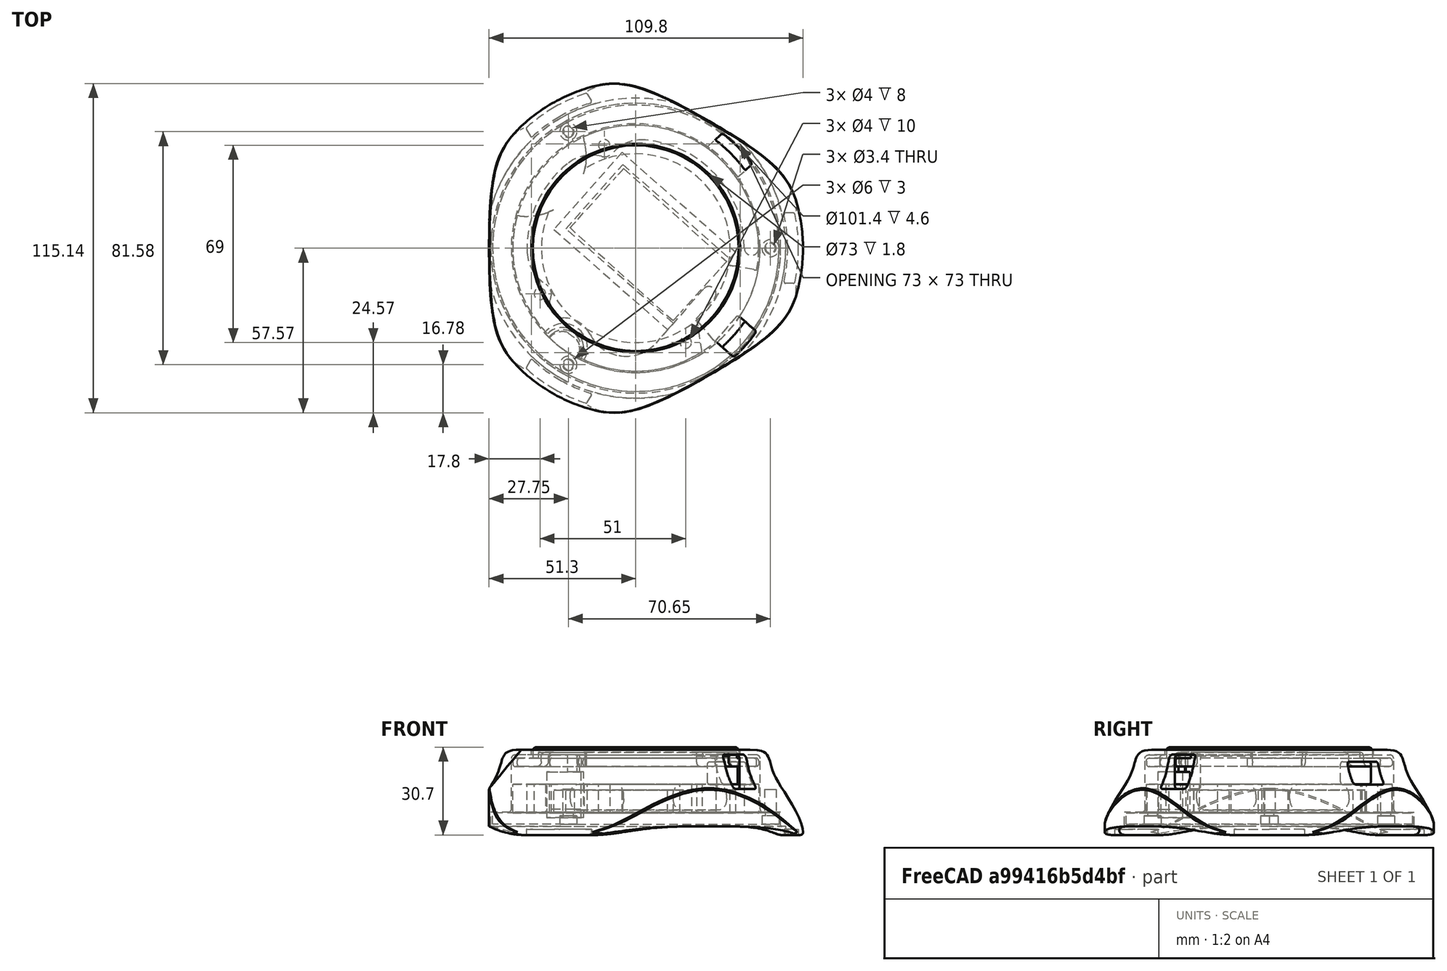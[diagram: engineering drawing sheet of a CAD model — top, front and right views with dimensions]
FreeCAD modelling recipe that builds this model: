
FCSTD DOCUMENT  (FreeCAD 1.0R39109 (Git))
Label: slimCasing
License: All rights reserved
LicenseURL: https://en.wikipedia.org/wiki/All_rights_reserved
objects: Sketcher::SketchObject×15, PartDesign::Pocket×9, PartDesign::Pad×6, PartDesign::SubShapeBinder×5, PartDesign::Body×4, PartDesign::Plane×4, Mesh::Feature×1, PartDesign::Revolution×1, PartDesign::Fillet×1, PartDesign::AdditivePipe×1, PartDesign::Mirrored×1, PartDesign::PolarPattern×1
note: 101 computed .brp shape members not serialized (recipe doc carries the construction recipe); baked Part::Feature solids carry a one-line shape summary decoded from their .brp

FEATURE [Sketcher::SketchObject] Sketch
  ArcFitTolerance = 1e-06
  AttachmentSupport = -> [XZ_Plane]
  FullyConstrained = true
  MakeInternals = false
  MapMode = 5
  Placement = pos=(0,0,0) rot=(1,0,0;1.5708rad)
  sketch-geometry (17):
    g0: LineSegment StartX=-36 StartY=12 StartZ=0 EndX=-36 EndY=9.5 EndZ=0
    g1: LineSegment StartX=-36 StartY=9.5 StartZ=0 EndX=-42 EndY=9.5 EndZ=0
    g2: LineSegment StartX=-43 StartY=8.5 StartZ=0 EndX=-43 EndY=7.5 EndZ=0
    g3: LineSegment StartX=-42 StartY=6.5 StartZ=0 EndX=-34.8 EndY=6.5 EndZ=0
    g4: LineSegment StartX=-33 StartY=8.3 StartZ=0 EndX=-33 EndY=10.2 EndZ=0
    g5: LineSegment StartX=-31.7 StartY=11.5 StartZ=0 EndX=0 EndY=11.5 EndZ=0
    g6: LineSegment StartX=0 StartY=11.5 StartZ=0 EndX=0 EndY=13.3 EndZ=0
    g7: ArcOfCircle CenterX=-34.7 CenterY=12 CenterZ=0 NormalX=0 NormalY=0 NormalZ=1 AngleXU=0 Radius=1.3 StartAngle=1.5708 EndAngle=3.14159
    g8: ArcOfCircle CenterX=-31.7 CenterY=10.2 CenterZ=0 NormalX=0 NormalY=0 NormalZ=1 AngleXU=0 Radius=1.3 StartAngle=1.5708 EndAngle=3.14159
    g9: GeomPoint [constr] X=-33 Y=11.5 Z=0
    g10: GeomPoint [constr] X=-36 Y=9.5 Z=0
    g11: ArcOfCircle CenterX=-34.8 CenterY=8.3 CenterZ=0 NormalX=0 NormalY=0 NormalZ=1 AngleXU=0 Radius=1.8 StartAngle=4.71239 EndAngle=6.28319
    g12: GeomPoint [constr] X=-33 Y=6.5 Z=0
    g13: ArcOfCircle CenterX=-42 CenterY=8.5 CenterZ=0 NormalX=0 NormalY=0 NormalZ=1 AngleXU=0 Radius=1 StartAngle=1.5708 EndAngle=3.14159
    g14: GeomPoint [constr] X=-43 Y=9.5 Z=0
    g15: ArcOfCircle CenterX=-42 CenterY=7.5 CenterZ=0 NormalX=0 NormalY=0 NormalZ=1 AngleXU=0 Radius=1 StartAngle=3.14159 EndAngle=4.71239
    g16: LineSegment StartX=-34.7 StartY=13.3 StartZ=0 EndX=0 EndY=13.3 EndZ=0
  constraints (41):
    c: Vertical(g0)
    c: Horizontal(g1)
    c: Vertical(g2)
    c: Horizontal(g3)
    c: Vertical(g4)
    c: Horizontal(g5)
    c: Coincident(g5,g6)
    c: Vertical(g6)
    c: DistanceY(g10,g9) = 2
    c: Distance(g10,g14) = 7
    c: DistanceX(g10,g9) = 3
    c: DistanceX(g9,g5) = 33
    c: DistanceY(g-1,g5) = 11.5
    c: Tangent(g0,g7) = -1.5708
    c: PointOnObject(g9,g4)
    c: PointOnObject(g9,g5)
    c: Tangent(g4,g8) = 1.5708
    c: Tangent(g5,g8) = 1.5708
    c: PointOnObject(g12,g3)
    c: PointOnObject(g12,g4)
    c: Tangent(g3,g11) = -1.5708
    c: Tangent(g4,g11) = -1.5708
    c: PointOnObject(g14,g2)
    c: PointOnObject(g14,g1)
    c: Tangent(g2,g13) = -1.5708
    c: Tangent(g1,g13) = -1.5708
    c: Tangent(g2,g15) = -1.5708
    c: Tangent(g3,g15) = -1.5708
    c: Equal(g7,g8)
    c: Coincident(g1,g10)
    c: Coincident(g0,g1)
    c: DistanceY(g0,g0) = 2.5
    c: Radius(g11) = 1.8
    c: Equal(g13,g15)
    c: Radius(g13) = 1
    c: PointOnObject(g5,g-2)
    c: DistanceY(g3,g1) = 3
    c: DistanceY(g7,g7) = 1.3
    c: Horizontal(g16)
    c: Coincident(g6,g16)
    c: Tangent(g7,g16) = 1.5708
FEATURE [Mesh::Feature] PCB_Board  label="PCB Board"
  Placement = pos=(-64.6,63.9,0) rot=(0,0,1;0rad)
FEATURE [PartDesign::Revolution] Revolution
  Angle = 360
  Angle2 = 60
  Axis = (0,2e-16,1)
  Base = (0,0,0)
  Placement = pos=(0,0,0) rot=(1,0,0;1.5708rad)
  Profile = -> Sketch
  ReferenceAxis = -> Sketch [V_Axis]
  Refine = true
  Suppressed = false
  Type = 0
FEATURE [Sketcher::SketchObject] Sketch001
  ArcFitTolerance = 1e-06
  AttachmentSupport = -> [Revolution]
  FullyConstrained = false
  MakeInternals = false
  MapMode = 5
  Placement = pos=(0,1.4e-15,6.5) rot=(1,0,0;3.14159rad)
  sketch-geometry (12):
    g0: ArcOfCircle CenterX=25.2748 CenterY=34.7877 CenterZ=0 NormalX=0 NormalY=0 NormalZ=1 AngleXU=0 Radius=6.2 StartAngle=2.58543 EndAngle=5.58271
    g1: ArcOfCircle CenterX=0 CenterY=0 CenterZ=0 NormalX=0 NormalY=0 NormalZ=1 AngleXU=0 Radius=43 StartAngle=0.798167 EndAngle=1.08679
    g2: LineSegment [constr] StartX=25.2748 StartY=34.7877 StartZ=0 EndX=0 EndY=0 EndZ=0
    g3: ArcOfCircle CenterX=-42.4024 CenterY=26.496 CenterZ=0 NormalX=0 NormalY=0 NormalZ=1 AngleXU=0 Radius=21 StartAngle=4.70073 EndAngle=6.74863
    g4: ArcOfCircle CenterX=0 CenterY=0 CenterZ=0 NormalX=0 NormalY=0 NormalZ=1 AngleXU=0 Radius=43 StartAngle=2.15278 EndAngle=3.0134
    g5: LineSegment [constr] StartX=0 StartY=0 StartZ=0 EndX=-42.4024 EndY=26.496 EndZ=0
    g6: LineSegment [constr] StartX=0 StartY=0 StartZ=0 EndX=31.9552 EndY=-28.7726 EndZ=0
    g7: LineSegment StartX=39.7845 StartY=-16.3155 StartZ=0 EndX=30.5323 EndY=-12.5212 EndZ=0
    g8: LineSegment StartX=20.3847 StartY=-37.8611 StartZ=0 EndX=15.6441 EndY=-29.0562 EndZ=0
    g9: ArcOfCircle CenterX=0 CenterY=0 CenterZ=0 NormalX=0 NormalY=0 NormalZ=1 AngleXU=0 Radius=33 StartAngle=5.20629 EndAngle=5.894
    g10: ArcOfCircle CenterX=0 CenterY=0 CenterZ=0 NormalX=0 NormalY=0 NormalZ=1 AngleXU=0 Radius=43 StartAngle=5.20629 EndAngle=5.894
    g11: LineSegment [constr] StartX=15.6441 StartY=-29.0562 StartZ=0 EndX=30.5323 EndY=-12.5212 EndZ=0
  constraints (20):
    c: Coincident(g1,g0)
    c: Coincident(g1,g0)
    c: Coincident(g2,g0)
    c: Angle(g-1,g2) = 0.942478
    c: Coincident(g4,g3)
    c: Coincident(g4,g3)
    c: Radius(g3) = 21
    c: Coincident(g5,g3)
    c: Distance(g5,g5) = 50
    c: Angle(g5,g-1) = 0.558505
    c: Coincident(g9,g7)
    c: Coincident(g9,g8)
    c: Distance(g7,g7) = 10
    c: Angle(g6,g-1) = 0.733038
    c: Coincident(g10,g7)
    c: Coincident(g10,g8)
    c: Coincident(g11,g8)
    c: Coincident(g11,g7)
    c: Perpendicular(g6,g11)
    c: Distance(g11,g11) = 22.25
FEATURE [Sketcher::SketchObject] Sketch027
  ArcFitTolerance = 0
  FullyConstrained = true
  MakeInternals = false
  MapMode = 5
  sketch-geometry (4):
    g0: LineSegment StartX=-24.25 StartY=14 StartZ=0 EndX=24.25 EndY=14 EndZ=0
    g1: LineSegment StartX=24.25 StartY=14 StartZ=0 EndX=24.25 EndY=-14 EndZ=0
    g2: LineSegment StartX=24.25 StartY=-14 StartZ=0 EndX=-24.25 EndY=-14 EndZ=0
    g3: LineSegment StartX=-24.25 StartY=-14 StartZ=0 EndX=-24.25 EndY=14 EndZ=0
  constraints (11):
    c: Coincident(g0,g1)
    c: Coincident(g1,g2)
    c: Coincident(g2,g3)
    c: Coincident(g3,g0)
    c: Horizontal(g0)
    c: Horizontal(g2)
    c: Vertical(g1)
    c: Vertical(g3)
    c: Symmetric(g0,g1,g-1)
    c: DistanceX(g0,g0) = 48.5
    c: DistanceY(g1,g1) = 28
FEATURE [PartDesign::Pad] Pad004
  Direction = (0,0,1)
  Length = 9
  Length2 = 10
  Profile = -> Sketch027
  ReferenceAxis = -> Sketch027 [N_Axis]
  Suppressed = false
  Type = 0
FEATURE [PartDesign::Fillet] Fillet002
  Base = -> Pad004 [Edge4,Edge3,Edge10,Edge9]
  BaseFeature = -> Pad004
  Radius = 4
  SupportTransform = false
  Suppressed = false
  UseAllEdges = false
FEATURE [PartDesign::Body] Body005  label="Batterie"
  AllowCompound = false
  Group = -> [Sketch027,Pad004,Fillet002]
  Placement = pos=(4.42123,1.23614,-9.3) rot=(0,0,1;5.5484rad)
  Tip = -> Fillet002
FEATURE [Sketcher::SketchObject] Sketch032
  ArcFitTolerance = 1e-06
  FullyConstrained = false
  MakeInternals = false
  MapMode = 5
  sketch-geometry (34):
    g0: Circle CenterX=17.5 CenterY=-33 CenterZ=0 NormalX=0 NormalY=0 NormalZ=1 AngleXU=0 Radius=2
    g1: Circle CenterX=-33.5 CenterY=-16 CenterZ=0 NormalX=0 NormalY=0 NormalZ=1 AngleXU=0 Radius=2
    g2: Circle CenterX=-11 CenterY=36 CenterZ=0 NormalX=0 NormalY=0 NormalZ=1 AngleXU=0 Radius=2
    g3: Circle [constr] CenterX=0 CenterY=0 CenterZ=0 NormalX=0 NormalY=0 NormalZ=1 AngleXU=0 Radius=32.5
    g4: Circle [constr] CenterX=0 CenterY=0 CenterZ=0 NormalX=0 NormalY=0 NormalZ=1 AngleXU=0 Radius=43
    g5: GeomPoint [constr] X=-11 Y=36 Z=0
    g6: LineSegment [constr] StartX=-12.5654 StartY=41.1231 StartZ=0 EndX=0 EndY=0 EndZ=0
    g7: LineSegment [constr] StartX=0 StartY=0 StartZ=0 EndX=-38.8021 EndY=-18.5309 EndZ=0
    g8: GeomPoint [constr] X=-33.5 Y=-16 Z=0
    g9: GeomPoint [constr] X=17.5 Y=-33 Z=0
    g10: LineSegment [constr] StartX=20.1456 StartY=-37.9889 StartZ=0 EndX=0 EndY=0 EndZ=0
    g11: ArcOfCircle CenterX=0 CenterY=0 CenterZ=0 NormalX=0 NormalY=0 NormalZ=1 AngleXU=0 Radius=43 StartAngle=4.27973 EndAngle=5.28201
    g12: ArcOfCircle CenterX=-25.2748 CenterY=-34.7877 CenterZ=0 NormalX=0 NormalY=0 NormalZ=1 AngleXU=0 Radius=8.4 StartAngle=5.7527 EndAngle=8.69863
    g13: ArcOfCircle CenterX=-25.2748 CenterY=-34.7877 CenterZ=0 NormalX=0 NormalY=0 NormalZ=1 AngleXU=0 Radius=10.4 StartAngle=0.461307 EndAngle=1.57014
    g14: ArcOfCircle CenterX=0 CenterY=0 CenterZ=0 NormalX=0 NormalY=0 NormalZ=1 AngleXU=0 Radius=43 StartAngle=1e-16 EndAngle=3.88841
    g15: LineSegment [constr] StartX=0 StartY=0 StartZ=0 EndX=-25.2748 EndY=-34.7877 EndZ=0
    g16: ArcOfCircle [constr] CenterX=0 CenterY=0 CenterZ=0 NormalX=0 NormalY=0 NormalZ=1 AngleXU=0 Radius=38 StartAngle=1.48247 EndAngle=5.30728
    g17: ArcOfCircle CenterX=-11 CenterY=36 CenterZ=0 NormalX=0 NormalY=0 NormalZ=1 AngleXU=0 Radius=4 StartAngle=4.4615 EndAngle=5.55637
    g18: ArcOfCircle CenterX=-15.3694 CenterY=18.951 CenterZ=0 NormalX=0 NormalY=0 NormalZ=1 AngleXU=0 Radius=13.6 StartAngle=1.31991 EndAngle=2.25221
    g19: ArcOfCircle CenterX=-33.5 CenterY=-16 CenterZ=0 NormalX=0 NormalY=0 NormalZ=1 AngleXU=0 Radius=4 StartAngle=5.8858 EndAngle=7.30937
    g20: ArcOfCircle CenterX=-24.3816 CenterY=-0.946243 CenterZ=0 NormalX=0 NormalY=0 NormalZ=1 AngleXU=0 Radius=13.6 StartAngle=3.18038 EndAngle=4.16777
    g21: ArcOfCircle CenterX=0 CenterY=0 CenterZ=0 NormalX=0 NormalY=0 NormalZ=1 AngleXU=0 Radius=38 StartAngle=2.25221 EndAngle=3.18038
    g22: ArcOfCircle CenterX=-25.2647 CenterY=-19.4565 CenterZ=0 NormalX=0 NormalY=0 NormalZ=1 AngleXU=0 Radius=4.93127 StartAngle=2.74421 EndAngle=4.71173
    g23: ArcOfCircle CenterX=-3.17343 CenterY=-24.1928 CenterZ=0 NormalX=0 NormalY=0 NormalZ=1 AngleXU=0 Radius=13.6 StartAngle=4.58196 EndAngle=5.56057
    g24: ArcOfCircle CenterX=-3.78345 CenterY=-24.1049 CenterZ=0 NormalX=0 NormalY=0 NormalZ=1 AngleXU=0 Radius=13.6 StartAngle=3.6029 EndAngle=4.5567
    g25: ArcOfCircle CenterX=0 CenterY=0 CenterZ=0 NormalX=0 NormalY=0 NormalZ=1 AngleXU=0 Radius=38 StartAngle=4.5567 EndAngle=4.58196
    g26: ArcOfCircle CenterX=0 CenterY=0 CenterZ=0 NormalX=0 NormalY=0 NormalZ=1 AngleXU=0 Radius=38 StartAngle=1e-16 EndAngle=1.48247
    g27: ArcOfCircle CenterX=40.5 CenterY=4.4e-15 CenterZ=0 NormalX=0 NormalY=0 NormalZ=1 AngleXU=0 Radius=2.5 StartAngle=3.14159 EndAngle=6.28319
    g28: ArcOfCircle CenterX=2.15235 CenterY=24.3049 CenterZ=0 NormalX=0 NormalY=0 NormalZ=1 AngleXU=0 Radius=13.6 StartAngle=1.48247 EndAngle=2.41477
    g29: LineSegment [constr] StartX=40.5 StartY=4.4e-15 StartZ=0 EndX=0 EndY=0 EndZ=0
    g30: LineSegment StartX=23.1906 StartY=-36.2104 StartZ=0 EndX=21.3491 EndY=-24.5044 EndZ=0
    g31: LineSegment StartX=21.3491 StartY=-24.5044 StartZ=0 EndX=27.4734 EndY=-17.5584 EndZ=0
    g32: ArcOfCircle CenterX=25.5982 CenterY=-15.905 CenterZ=0 NormalX=0 NormalY=0 NormalZ=1 AngleXU=0 Radius=2.5 StartAngle=5.56057 EndAngle=8.70217
    g33: LineSegment StartX=23.723 StartY=-14.2517 StartZ=0 EndX=7.02767 EndY=-33.1871 EndZ=0
  constraints (84):
    c: Equal(g0,g2)
    c: Equal(g2,g1)
    c: Diameter(g2) = 4
    c: DistanceX(g1,g-1) = 33.5
    c: DistanceY(g1,g-1) = 16
    c: DistanceX(g2) = -11
    c: DistanceY(g2) = 36
    c: DistanceX(g0) = 17.5
    c: DistanceY(g0) = -33
    c: Coincident(g3,g-1)
    c: Coincident(g4,g3)
    c: Diameter(g4) = 86
    c: Diameter(g3) = 65
    c: Coincident(g2,g5)
    c: PointOnObject(g6,g4)
    c: Coincident(g6,g3)
    c: PointOnObject(g2,g6)
    c: Coincident(g7,g3)
    c: PointOnObject(g7,g4)
    c: Coincident(g8,g1)
    c: Coincident(g9,g0)
    c: PointOnObject(g10,g4)
    c: Coincident(g10,g3)
    c: PointOnObject(g0,g10)
    c: PointOnObject(g11,g4)
    c: Distance(g23,g4) = 5
    c: Coincident(g11,g3)
    c: PointOnObject(g12,g4)
    c: Coincident(g12,g11)
    c: PointOnObject(g12,g4)
    c: Coincident(g13,g12)
    c: Coincident(g14,g3)
    c: Coincident(g14,g12)
    c: Distance(g12,g13) = 2
    c: Radius(g12) = 8.4
    c: Coincident(g15,g3)
    c: Coincident(g15,g12)
    c: Angle(g-1,g15) = 0.942478
    c: Coincident(g16,g3)
    c: Coincident(g17,g2)
    c: PointOnObject(g18,g16)
    c: PointOnObject(g23,g16)
    c: Tangent(g18,g17) = 1.5708
    c: Coincident(g19,g1)
    c: Distance(g19,g1) = 2
    c: Tangent(g20,g19) = 1.5708
    c: Coincident(g21,g3)
    c: Tangent(g21,g20) = -1.5708
    c: Tangent(g21,g18) = -1.5708
    c: Tangent(g22,g13) = 1.5708
    c: Tangent(g22,g19) = 1.5708
    c: Coincident(g25,g3)
    c: Tangent(g24,g13) = 1.5708
    c: Tangent(g25,g24) = -1.5708
    c: Equal(g23,g24)
    c: Equal(g24,g20)
    c: Equal(g20,g18)
    c: Radius(g18) = 13.6
    c: Tangent(g25,g23) = -1.5708
    c: Tangent(g22,g20)
    c: Coincident(g26,g3)
    c: Coincident(g26,g16)
    c: Tangent(g27,g26) = 1.5708
    c: Tangent(g27,g14) = -1.5708
    c: Coincident(g28,g16)
    c: Tangent(g26,g28)
    c: Equal(g28,g18)
    c: Coincident(g29,g27)
    c: Coincident(g29,g3)
    c: Angle(g29,g-2) = 1.5708
    c: Tangent(g28,g17) = 1.5708
    c: Distance(g17,g2) = 2
    c: Coincident(g31,g30)
    c: Tangent(g31,g32) = -1.5708
    c: PointOnObject(g30,g3)
    c: Tangent(g33,g23) = 1.5708
    c: Tangent(g33,g32) = -1.5708
    c: Coincident(g11,g30)
    c: Parallel(g31,g33)
    c: DistanceX(g32) = 25.5982
    c: DistanceY(g32) = -15.905
    c: Distance(g33,g31) = 5
    c: Angle(g-2,g30) = 0.156032
    c: Distance(g30,g30) = 11.85
FEATURE [PartDesign::Pad] Pad007
  Direction = (0,0,1)
  Length = 10
  Length2 = 10
  Profile = -> Sketch032
  ReferenceAxis = -> Sketch032 [N_Axis]
  Refine = true
  Reversed = true
  Suppressed = false
  Type = 0
FEATURE [Sketcher::SketchObject] Sketch033
  ArcFitTolerance = 1e-06
  AttachmentSupport = -> [Pad007]
  FullyConstrained = true
  MakeInternals = false
  MapMode = 5
  Placement = pos=(0,0,-10) rot=(1,0,0;3.14159rad)
  sketch-geometry (12):
    g0: Circle CenterX=-7.1e-15 CenterY=0 CenterZ=0 NormalX=0 NormalY=0 NormalZ=1 AngleXU=0 Radius=51.1
    g1: Circle CenterX=-23.55 CenterY=-40.7898 CenterZ=0 NormalX=0 NormalY=0 NormalZ=1 AngleXU=0 Radius=3
    g2: Circle CenterX=-23.55 CenterY=-40.7898 CenterZ=0 NormalX=0 NormalY=0 NormalZ=1 AngleXU=0 Radius=1.7
    g3: LineSegment [constr] StartX=-23.55 StartY=-40.7898 StartZ=0 EndX=-7.1e-15 EndY=0 EndZ=0
    g4: Circle CenterX=-23.55 CenterY=40.7898 CenterZ=0 NormalX=0 NormalY=0 NormalZ=1 AngleXU=0 Radius=3
    g5: Circle CenterX=-23.55 CenterY=40.7898 CenterZ=0 NormalX=0 NormalY=0 NormalZ=1 AngleXU=0 Radius=1.7
    g6: Circle CenterX=47.1 CenterY=0 CenterZ=0 NormalX=0 NormalY=0 NormalZ=1 AngleXU=0 Radius=1.7
    g7: Circle CenterX=47.1 CenterY=0 CenterZ=0 NormalX=0 NormalY=0 NormalZ=1 AngleXU=0 Radius=3
    g8: Circle [constr] CenterX=-7.1e-15 CenterY=0 CenterZ=0 NormalX=0 NormalY=0 NormalZ=1 AngleXU=0 Radius=47.1
    g9: LineSegment [constr] StartX=47.1 StartY=0 StartZ=0 EndX=-7.1e-15 EndY=0 EndZ=0
    g10: LineSegment [constr] StartX=-23.55 StartY=40.7898 StartZ=0 EndX=-7.1e-15 EndY=0 EndZ=0
    g11: Circle CenterX=-7.1e-15 CenterY=0 CenterZ=0 NormalX=0 NormalY=0 NormalZ=1 AngleXU=0 Radius=50.1
  constraints (27):
    c: Coincident(g0,g-1)
    c: Radius(g0) = 51.1
    c: Diameter(g1) = 6
    c: Coincident(g2,g1)
    c: Diameter(g2) = 3.4
    c: Coincident(g3,g1)
    c: Coincident(g3,g0)
    c: Distance(g1,g0) = 4
    c: Coincident(g5,g4)
    c: Coincident(g7,g6)
    c: Equal(g7,g1)
    c: Equal(g1,g4)
    c: Equal(g5,g2)
    c: Equal(g2,g6)
    c: Coincident(g8,g0)
    c: PointOnObject(g1,g8)
    c: PointOnObject(g6,g8)
    c: Coincident(g9,g6)
    c: Coincident(g9,g0)
    c: PointOnObject(g6,g-1)
    c: PointOnObject(g4,g8)
    c: Coincident(g10,g4)
    c: Coincident(g10,g0)
    c: Angle(g9,g10) = 2.0944
    c: Angle(g10,g3) = 2.0944
    c: Coincident(g11,g0)
    c: Tangent(g11,g7)
FEATURE [Sketcher::SketchObject] Sketch035
  ArcFitTolerance = 1e-06
  FullyConstrained = true
  MakeInternals = false
  MapMode = 5
  Placement = pos=(0,0,-10) rot=(0,0,1;0rad)
  sketch-geometry (9):
    g0: LineSegment StartX=13.1319 StartY=-26.2638 StartZ=0 EndX=-24.3722 EndY=6.80349 EndZ=0
    g1: LineSegment StartX=-24.3722 StartY=6.80349 StartZ=0 EndX=-4.53179 EndY=29.3059 EndZ=0
    g2: LineSegment StartX=-4.53179 StartY=29.3059 StartZ=0 EndX=32.9723 EndY=-3.76138 EndZ=0
    g3: LineSegment StartX=32.9723 StartY=-3.76138 StartZ=0 EndX=34.9563 EndY=-1.51113 EndZ=0
    g4: LineSegment [constr] StartX=23.723 StartY=-14.2517 StartZ=0 EndX=32.9723 EndY=-3.76138 EndZ=0
    g5: LineSegment StartX=34.9563 StartY=-1.51113 StartZ=0 EndX=-4.79799 EndY=33.5402 EndZ=0
    g6: LineSegment StartX=-4.79799 StartY=33.5402 StartZ=0 EndX=-28.6064 EndY=6.53728 EndZ=0
    g7: LineSegment StartX=-28.6064 StartY=6.53728 StartZ=0 EndX=11.1479 EndY=-28.5141 EndZ=0
    g8: LineSegment StartX=11.1479 StartY=-28.5141 StartZ=0 EndX=13.1319 EndY=-26.2638 EndZ=0
  constraints (26):
    c: PointOnObject(g0,g-3)
    c: Coincident(g1,g0)
    c: Perpendicular(g0,g1)
    c: Perpendicular(g0,g-3)
    c: Coincident(g2,g1)
    c: Coincident(g3,g2)
    c: Perpendicular(g2,g3)
    c: Distance(g3,g3) = 3
    c: Distance(g1,g1) = 30
    c: Parallel(g2,g0)
    c: Distance(g0,g0) = 50
    c: Distance(g0,g-3) = 9.23
    c: Coincident(g4,g-3)
    c: Coincident(g4,g2)
    c: Parallel(g4,g-3)
    c: Coincident(g5,g3)
    c: Coincident(g6,g5)
    c: Coincident(g7,g6)
    c: PointOnObject(g7,g-3)
    c: Coincident(g8,g7)
    c: Coincident(g8,g0)
    c: Parallel(g6,g1)
    c: Parallel(g7,g0)
    c: Parallel(g5,g2)
    c: Distance(g6,g1) = 3
    c: Distance(g7,g0) = 3
FEATURE [PartDesign::Pad] Pad009
  BaseFeature = -> Pad007
  Direction = (0,0,1)
  Length = 8
  Length2 = 10
  Profile = -> Sketch035
  ReferenceAxis = -> Sketch035 [N_Axis]
  Refine = true
  Suppressed = false
  Type = 0
FEATURE [PartDesign::Plane] DatumPlane005
  AttachmentOffset = pos=(0,0,0) rot=(0,-1,0;1.0472rad)
  AttachmentSupport = -> [XZ_Plane006]
  Length = 135.747
  MapMode = 5
  Placement = pos=(0,0,0) rot=(0.774597,-0.447214,-0.447214;1.82348rad)
  ResizeMode = 0
  Width = 65.5074
FEATURE [Sketcher::SketchObject] Sketch045
  ArcFitTolerance = 1e-06
  AttachmentSupport = -> [XZ_Plane006]
  FullyConstrained = false
  MakeInternals = false
  MapMode = 5
  Placement = pos=(0,0,0) rot=(1,0,0;1.5708rad)
  sketch-geometry (38):
    g0: LineSegment [constr] StartX=-36.5 StartY=11.8 StartZ=0 EndX=-36.5 EndY=10 EndZ=0
    g1: LineSegment [constr] StartX=0 StartY=0 StartZ=0 EndX=-36 EndY=0 EndZ=0
    g2: LineSegment [constr] StartX=0 StartY=0 StartZ=0 EndX=-43 EndY=0 EndZ=0
    g3: LineSegment [constr] StartX=-36.5 StartY=11.8 StartZ=0 EndX=-40.0197 EndY=11.8 EndZ=0
    g4: LineSegment [constr] StartX=0 StartY=0 StartZ=0 EndX=0 EndY=-10 EndZ=0
    g5: LineSegment [constr] StartX=0 StartY=-10 StartZ=0 EndX=-43.5 EndY=-10 EndZ=0
    g6: LineSegment [constr] StartX=-43.5 StartY=-10 StartZ=0 EndX=-43.5 EndY=-2 EndZ=0
    g7: LineSegment [constr] StartX=-43.5 StartY=-2 StartZ=0 EndX=-43.5 EndY=-10 EndZ=0
    g8: LineSegment [constr] StartX=-45.3 StartY=-10 StartZ=0 EndX=-43.5 EndY=-10 EndZ=0
    g9: LineSegment [constr] StartX=-45.3 StartY=8.7 StartZ=0 EndX=-45.3 EndY=-10 EndZ=0
    g10-g14: Circle [constr] x5 (B-spline internal-alignment scaffolding for g15; pole/knot coordinates omitted)
    g15: BSplineCurve PolesCount=5 KnotsCount=3 Degree=3 IsPeriodic=0
    g16: GeomPoint [constr] X=-40.0197 Y=11.8 Z=0
    g17: GeomPoint [constr] X=-48.1349 Y=3.93953 Z=0
    g18: GeomPoint [constr] X=-58.5 Y=-17 Z=0
    g19: ArcOfCircle CenterX=-42.2 CenterY=8.7 CenterZ=0 NormalX=0 NormalY=0 NormalZ=1 AngleXU=0 Radius=1.3 StartAngle=1.5708 EndAngle=3.14159
    g20: LineSegment StartX=-40.0197 StartY=11.8 StartZ=0 EndX=-36.5 EndY=11.8 EndZ=0
    g21: LineSegment StartX=-36.5 StartY=11.8 StartZ=0 EndX=-36.5 EndY=10 EndZ=0
    g22: LineSegment StartX=-36.5 StartY=10 StartZ=0 EndX=-42.2 EndY=10 EndZ=0
    g23: LineSegment StartX=-43.5 StartY=-10 StartZ=0 EndX=-50.7 EndY=-10 EndZ=0
    g24: LineSegment [constr] StartX=-45.1 StartY=-10 StartZ=0 EndX=-45.1 EndY=-3 EndZ=0
    g25: LineSegment [constr] StartX=-45.1 StartY=-3 StartZ=0 EndX=-49.1 EndY=-3 EndZ=0
    g26: LineSegment [constr] StartX=-49.1 StartY=-3 StartZ=0 EndX=-49.1 EndY=-10 EndZ=0
    g27: Circle [constr] CenterX=-58.5 CenterY=-17 CenterZ=0 NormalX=0 NormalY=0 NormalZ=1 AngleXU=0 Radius=1
    g28: Circle [constr] CenterX=-58.5 CenterY=-18 CenterZ=0 NormalX=0 NormalY=0 NormalZ=1 AngleXU=0 Radius=1
    g29: Circle [constr] CenterX=-57.5 CenterY=-18 CenterZ=0 NormalX=0 NormalY=0 NormalZ=1 AngleXU=0 Radius=1
    g30: BSplineCurve PolesCount=3 KnotsCount=2 Degree=2 IsPeriodic=0
    g31: GeomPoint [constr] X=-58.5 Y=-17 Z=0
    g32: GeomPoint [constr] X=-57.5 Y=-18 Z=0
    g33: LineSegment StartX=-57.5 StartY=-18 StartZ=0 EndX=-52.5 EndY=-18 EndZ=0
    g34: LineSegment StartX=-43.5 StartY=8.7 StartZ=0 EndX=-43.5 EndY=-10 EndZ=0
    g35: LineSegment StartX=-52.5 StartY=-18 StartZ=0 EndX=-52.5 EndY=-15 EndZ=0
    g36: LineSegment StartX=-50.7 StartY=-10 StartZ=0 EndX=-50.7 EndY=-15 EndZ=0
    g37: LineSegment StartX=-50.7 StartY=-15 StartZ=0 EndX=-52.5 EndY=-15 EndZ=0
  constraints (94):
    c: Vertical(g0)
    c: PointOnObject(g1,g-2)
    c: Horizontal(g1)
    c: DistanceX(g1,g1) = 36
    c: DistanceX(g0,g1) = 0.5
    c: Distance(g0,g0) = 1.8
    c: PointOnObject(g2,g-2)
    c: Horizontal(g2)
    c: DistanceX(g2,g2) = 43
    c: DistanceX(g6,g2) = 0.5
    c: PointOnObject(g2,g-1)
    c: PointOnObject(g1,g-1)
    c: Coincident(g3,g0)
    c: Horizontal(g3)
    c: DistanceY(g-1,g0) = 10
    c: Coincident(g4,g1)
    c: PointOnObject(g4,g-2)
    c: DistanceY(g4,g-1) = 10
    c: Coincident(g5,g4)
    c: Horizontal(g5)
    c: Coincident(g7,g5)
    c: Vertical(g6)
    c: DistanceY(g6,g2) = 2
    c: Coincident(g7,g6)
    c: Coincident(g8,g5)
    c: Horizontal(g8)
    c: Coincident(g9,g8)
    c: Vertical(g9)
    c: Distance(g8,g8) = 1.8
    c: DistanceX(g8,g-1) = 45.3
    c: Distance(g3,g-2) = 40.0197
    c: Weight(g10) = 1
    c: Equal(g10,g14)
    c: InternalAlignment(g10-g14 -> g15) x5
    c: InternalAlignment(g16,g15)
    c: InternalAlignment(g17,g15)
    c: InternalAlignment(g18,g15)
    c: Coincident(g10,g3)
    c: Horizontal(g11,g15)
    c: Horizontal(g19,g19)
    c: Vertical(g19,g19)
    c: Radius(g19) = 1.3
    c: Coincident(g20,g15)
    c: Coincident(g20,g0)
    c: Coincident(g21,g0)
    c: Coincident(g21,g0)
    c: Coincident(g22,g0)
    c: Coincident(g22,g19)
    c: Horizontal(g22)
    c: Coincident(g23,g5)
    c: Horizontal(g23)
    c: Weight(g13) = 0.5
    c: Weight(g11) = 2
    c: Vertical(g13,g15)
    c: Coincident(g24,g25)
    c: Coincident(g25,g26)
    c: Horizontal(g25)
    c: Vertical(g24)
    c: Vertical(g26)
    c: PointOnObject(g26,g23)
    c: DistanceX(g25,g25) = 4
    c: DistanceX(g23,g26) = 1.6
    c: DistanceX(g24,g5) = 1.6
    c: Coincident(g6,g5)
    c: Weight(g27) = 1
    c: Equal(g27,g28)
    c: Equal(g27,g29)
    c: InternalAlignment(g27,g30)
    c: InternalAlignment(g28,g30)
    c: InternalAlignment(g29,g30)
    c: InternalAlignment(g31,g30)
    c: InternalAlignment(g32,g30)
    c: Coincident(g27,g15)
    c: Horizontal(g30,g28)
    c: Vertical(g28,g30)
    c: Coincident(g33,g30)
    c: Horizontal(g33)
    c: DistanceX(g33,g33) = 5
    c: DistanceX(g30,g30) = 1
    c: DistanceY(g30,g30) = 1
    c: Weight(g12) = 1
    c: DistanceY(g26,g26) = 7
    c: Tangent(g34,g19) = -1.5708
    c: Coincident(g34,g5)
    c: Coincident(g35,g33)
    c: Vertical(g35)
    c: Coincident(g36,g23)
    c: Vertical(g36)
    c: Coincident(g37,g36)
    c: Coincident(g37,g35)
    c: Horizontal(g37)
    c: Distance(g37,g37) = 1.8
    c: DistanceY(g35,g35) = 3
    c: Distance(g36,g36) = 5
FEATURE [Sketcher::SketchObject] Sketch044
  ArcFitTolerance = 1e-06
  ExternalGeometry = -> [Sketch045]
  FullyConstrained = true
  MakeInternals = false
  sketch-geometry (1):
    g0: ArcOfCircle CenterX=0 CenterY=0 CenterZ=0 NormalX=0 NormalY=0 NormalZ=1 AngleXU=0 Radius=43.5 StartAngle=2.0944 EndAngle=3.14159
  constraints (3):
    c: Angle(g0) = 1.0472
    c: Coincident(g0,g-1)
    c: Coincident(g0,g-3)
FEATURE [PartDesign::AdditivePipe] AdditivePipe
  AuxilleryCurvelinear = true
  AuxillerySpineTangent = false
  Binormal = (0,0,0)
  Mode = 0
  Placement = pos=(0,0,0) rot=(1,0,0;1.5708rad)
  Profile = -> Sketch045
  Refine = true
  Spine = -> Sketch044
  SpineTangent = false
  Suppressed = false
  Transformation = 0
  Transition = 0
FEATURE [Sketcher::SketchObject] Sketch046
  ArcFitTolerance = 1e-06
  AttachmentSupport = -> [XY_Plane006]
  ExternalGeometry = -> [Sketch044,AdditivePipe,Sketch045]
  FullyConstrained = false
  MakeInternals = false
  MapMode = 5
  sketch-geometry (18):
    g0: ArcOfCircle [constr] CenterX=0 CenterY=0 CenterZ=0 NormalX=0 NormalY=0 NormalZ=1 AngleXU=0 Radius=104.589 StartAngle=1.9635 EndAngle=2.74889
    g1: LineSegment [constr] StartX=-73.9554 StartY=73.9554 StartZ=0 EndX=0 EndY=0 EndZ=0
    g2: LineSegment [constr] StartX=-96.6273 StartY=40.0244 StartZ=0 EndX=-40.0244 EndY=96.6273 EndZ=0
    g3: ArcOfCircle [constr] CenterX=0 CenterY=0 CenterZ=0 NormalX=0 NormalY=0 NormalZ=1 AngleXU=0 Radius=44.1 StartAngle=1.56696 EndAngle=3.14159
    g4-g8: Circle [constr] x5 (B-spline internal-alignment scaffolding for g9; pole/knot coordinates omitted)
    g9: BSplineCurve PolesCount=5 KnotsCount=3 Degree=3 IsPeriodic=0
    g10: GeomPoint [constr] X=-41.3657 Y=41.3657 Z=0
    g11: GeomPoint [constr] X=-48.6048 Y=23.0016 Z=0
    g12: GeomPoint [constr] X=-44.1 Y=0 Z=0
    g13: ArcOfCircle [constr] CenterX=0 CenterY=0 CenterZ=0 NormalX=0 NormalY=0 NormalZ=1 AngleXU=0 Radius=58.5 StartAngle=2.35619 EndAngle=3.14159
    g14: LineSegment [constr] StartX=-41.3657 StartY=41.3657 StartZ=0 EndX=-47.3272 EndY=35.4043 EndZ=0
    g15: LineSegment StartX=-44.1 StartY=5.4e-15 StartZ=0 EndX=-75 EndY=5.4e-15 EndZ=0
    g16: ArcOfCircle CenterX=0 CenterY=0 CenterZ=0 NormalX=0 NormalY=0 NormalZ=1 AngleXU=0 Radius=75 StartAngle=2.35619 EndAngle=3.14159
    g17: LineSegment StartX=-41.3657 StartY=41.3657 StartZ=0 EndX=-53.033 EndY=53.033 EndZ=0
  constraints (34):
    c: Angle(g0) = 0.785398
    c: Coincident(g0,g-1)
    c: PointOnObject(g1,g0)
    c: Coincident(g1,g0)
    c: Coincident(g2,g0)
    c: Coincident(g2,g0)
    c: Perpendicular(g2,g1)
    c: Angle(g1,g-1) = 0.785398
    c: Coincident(g3,g0)
    c: Weight(g4) = 1
    c: Equal(g4, g5-g8) x4
    c: InternalAlignment(g4-g8 -> g9) x5
    c: InternalAlignment(g10,g9)
    c: InternalAlignment(g11,g9)
    c: InternalAlignment(g12,g9)
    c: Coincident(g8,g3)
    c: Vertical(g7,g9)
    c: Coincident(g13,g0)
    c: Coincident(g13,g-6)
    c: PointOnObject(g13,g1)
    c: Coincident(g4,g13)
    c: Coincident(g14,g9)
    c: Coincident(g14,g5)
    c: Tangent(g14,g13)
    c: Coincident(g15,g9)
    c: PointOnObject(g15,g-1)
    c: Horizontal(g15)
    c: Coincident(g16,g0)
    c: Coincident(g16,g15)
    c: PointOnObject(g16,g1)
    c: Coincident(g17,g4)
    c: Coincident(g17,g16)
    c: Radius(g16) = 75
    c: DistanceX(g3,g-3) = 0.6
FEATURE [PartDesign::Pocket] Pocket008
  BaseFeature = -> AdditivePipe
  Direction = (0,0,-1)
  Length = 5
  Length2 = 5
  Midplane = true
  Placement = pos=(0,0,0) rot=(1,0,0;1.5708rad)
  Profile = -> Sketch046
  ReferenceAxis = -> Sketch046 [N_Axis]
  Refine = true
  Suppressed = false
  Type = 1
FEATURE [PartDesign::Plane] DatumPlane006
  AttachmentSupport = -> [Pocket008]
  Length = 133.53
  MapMode = 7
  Placement = pos=(-20.0098,34.658,11.8) rot=(-0.186157,0.694747,0.694747;3.50969rad)
  ResizeMode = 0
  Width = 65.3726
FEATURE [Sketcher::SketchObject] Sketch047
  ArcFitTolerance = 1e-06
  AttachmentSupport = -> [DatumPlane006]
  ExternalGeometry = -> [Pocket008]
  FullyConstrained = false
  MakeInternals = false
  MapMode = 5
  Placement = pos=(-20.0098,34.658,11.8) rot=(-0.186157,0.694747,0.694747;3.50969rad)
  sketch-geometry (10):
    g0: Circle [constr] CenterX=12.9092 CenterY=-29.8 CenterZ=0 NormalX=0 NormalY=0 NormalZ=1 AngleXU=0 Radius=1
    g1: Circle [constr] CenterX=21.0049 CenterY=-29.8 CenterZ=0 NormalX=0 NormalY=0 NormalZ=1 AngleXU=0 Radius=1
    g2: Circle [constr] CenterX=28.1337 CenterY=-26.8 CenterZ=0 NormalX=0 NormalY=0 NormalZ=1 AngleXU=0 Radius=1
    g3: BSplineCurve PolesCount=4 KnotsCount=2 Degree=3 IsPeriodic=0
    g4: GeomPoint [constr] X=12.9092 Y=-29.8 Z=0
    g5: GeomPoint [constr] X=40.9737 Y=-26.8 Z=0
    g6: LineSegment StartX=44.4271 StartY=-31.7175 StartZ=0 EndX=12.9092 EndY=-31.7175 EndZ=0
    g7: LineSegment StartX=12.9092 StartY=-29.8 StartZ=0 EndX=12.9092 EndY=-31.7175 EndZ=0
    g8: LineSegment StartX=40.9737 StartY=-26.8 StartZ=0 EndX=44.4271 EndY=-26.8 EndZ=0
    g9: LineSegment StartX=44.4271 StartY=-31.7175 StartZ=0 EndX=44.4271 EndY=-26.8 EndZ=0
  constraints (21):
    c: Weight(g0) = 1
    c: Equal(g0,g1)
    c: Equal(g0,g2)
    c: InternalAlignment(g0,g3)
    c: InternalAlignment(g1,g3)
    c: InternalAlignment(g2,g3)
    c: InternalAlignment(g4,g3)
    c: InternalAlignment(g5,g3)
    c: PointOnObject(g0,g-3)
    c: Horizontal(g2,g3)
    c: Horizontal(g1,g3)
    c: Horizontal(g6)
    c: Coincident(g7,g3)
    c: Coincident(g7,g6)
    c: Vertical(g7)
    c: Coincident(g8,g3)
    c: Horizontal(g8)
    c: Coincident(g9,g6)
    c: Coincident(g9,g8)
    c: Vertical(g9)
    c: Coincident(g8,g-4)
FEATURE [PartDesign::Pocket] Pocket001
  BaseFeature = -> Pocket008
  Direction = (0.5,-0.866025,0)
  Length = 5
  Length2 = 5
  Midplane = true
  Placement = pos=(0,0,0) rot=(1,0,0;1.5708rad)
  Profile = -> Sketch047
  ReferenceAxis = -> Sketch047 [N_Axis]
  Refine = true
  Suppressed = false
  Type = 1
FEATURE [Sketcher::SketchObject] Sketch048
  ArcFitTolerance = 1e-06
  FullyConstrained = true
  MakeInternals = false
  MapMode = 5
  Placement = pos=(0,2.2e-15,-10) rot=(1,0,0;3.14159rad)
  sketch-geometry (2):
    g0: LineSegment [constr] StartX=-25.35 StartY=-43.9075 StartZ=0 EndX=0 EndY=0 EndZ=0
    g1: Circle CenterX=-23.55 CenterY=-40.7898 CenterZ=0 NormalX=0 NormalY=0 NormalZ=1 AngleXU=0 Radius=2
  constraints (5):
    c: Coincident(g0,g-1)
    c: PointOnObject(g-3,g0)
    c: PointOnObject(g0,g-4)
    c: Diameter(g1) = 4
    c: Symmetric(g0,g-3,g1)
FEATURE [PartDesign::Pocket] Pocket009
  BaseFeature = -> Pocket001
  Direction = (0,1e-16,1)
  Length = 8
  Length2 = 5
  Placement = pos=(0,0,0) rot=(1,0,0;1.5708rad)
  Profile = -> Sketch048
  ReferenceAxis = -> Sketch048 [N_Axis]
  Refine = true
  Suppressed = false
  Type = 0
FEATURE [Sketcher::SketchObject] Sketch049
  ArcFitTolerance = 1e-06
  FullyConstrained = true
  MakeInternals = false
  MapMode = 5
  Placement = pos=(5.1e-15,4e-15,-18) rot=(1,0,0;3.14159rad)
  sketch-geometry (8):
    g0: ArcOfCircle CenterX=0 CenterY=0 CenterZ=0 NormalX=0 NormalY=0 NormalZ=1 AngleXU=0 Radius=56.9139 StartAngle=3.97977 EndAngle=4.39835
    g1: ArcOfCircle CenterX=0 CenterY=0 CenterZ=0 NormalX=0 NormalY=0 NormalZ=1 AngleXU=0 Radius=53.1597 StartAngle=3.96908 EndAngle=4.40904
    g2: LineSegment StartX=-38.1871 StartY=-41.5714 StartZ=0 EndX=-36.904 EndY=-39.2859 EndZ=0
    g3: LineSegment StartX=-16.8796 StartY=-53.8657 StartZ=0 EndX=-15.543 EndY=-51.611 EndZ=0
    g4: ArcOfCircle CenterX=-36.3808 CenterY=-39.5796 CenterZ=0 NormalX=0 NormalY=0 NormalZ=1 AngleXU=0 Radius=0.6 StartAngle=0.827485 EndAngle=2.63004
    g5: ArcOfCircle CenterX=-37.6639 CenterY=-41.8651 CenterZ=0 NormalX=0 NormalY=0 NormalZ=1 AngleXU=0 Radius=0.6 StartAngle=2.63004 EndAngle=3.97977
    g6: ArcOfCircle CenterX=-16.0591 CenterY=-51.3051 CenterZ=0 NormalX=0 NormalY=0 NormalZ=1 AngleXU=0 Radius=0.6 StartAngle=5.74807 EndAngle=7.55063
    g7: ArcOfCircle CenterX=-17.3957 CenterY=-53.5597 CenterZ=0 NormalX=0 NormalY=0 NormalZ=1 AngleXU=0 Radius=0.6 StartAngle=4.39835 EndAngle=5.74807
  constraints (20):
    c: Coincident(g0,g-1)
    c: Coincident(g1,g0)
    c: Tangent(g2,g4) = 1.5708
    c: Tangent(g1,g4) = 1.5708
    c: Tangent(g2,g5) = 1.5708
    c: Tangent(g0,g5) = -1.5708
    c: Tangent(g1,g6) = 1.5708
    c: Tangent(g3,g6) = -1.5708
    c: Tangent(g0,g7) = -1.5708
    c: Tangent(g3,g7) = -1.5708
    c: Equal(g6,g7)
    c: Equal(g7,g4)
    c: Equal(g4,g5)
    c: Radius(g4) = 0.6
    c: Distance(g0,g1) = 3.8
    c: Distance(g0,g1) = 3.8
    c: Distance(g1,g1) = 23.2
    c: Distance(g2,g3) = 24.6
    c: DistanceX(g1) = -15.8798
    c: DistanceY(g1) = -50.7325
FEATURE [PartDesign::Pocket] Pocket010
  BaseFeature = -> Pocket009
  Direction = (0,1e-16,1)
  Length = 2
  Length2 = 5
  Placement = pos=(0,0,0) rot=(1,0,0;1.5708rad)
  Profile = -> Sketch049
  ReferenceAxis = -> Sketch049 [N_Axis]
  Refine = true
  Suppressed = false
  Type = 0
FEATURE [PartDesign::Mirrored] Mirrored
  BaseFeature = -> Pocket010
  MirrorPlane = -> DatumPlane005
  Originals = -> [AdditivePipe,Pocket009,Pocket001,Pocket008,Pocket010]
  Placement = pos=(0,0,0) rot=(1,0,0;1.5708rad)
  Refine = true
  Suppressed = false
  TransformMode = 0
FEATURE [PartDesign::PolarPattern] PolarPattern
  Angle = 360
  Axis = -> Z_Axis006
  BaseFeature = -> Mirrored
  Mode = 0
  Occurrences = 3
  Offset = 120
  Placement = pos=(0,0,0) rot=(1,0,0;1.5708rad)
  Refine = true
  Suppressed = false
  TransformMode = 1
FEATURE [PartDesign::SubShapeBinder] Binder
  BindCopyOnChange = 0
  BindMode = 0
  ClaimChildren = false
  Context = -> Body002 [Binder.]
  Fuse = false
  MakeFace = true
  OffsetFill = false
  OffsetIntersection = false
  OffsetJoinType = 0
  OffsetOpenResult = false
  PartialLoad = false
  Refine = true
  Relative = true
  Support = -> [Sketch033[Edge8]]
  _Version = 2
FEATURE [PartDesign::SubShapeBinder] Binder001
  BindCopyOnChange = 0
  BindMode = 0
  ClaimChildren = false
  Context = -> Body002 [Binder001.]
  Fuse = false
  MakeFace = true
  OffsetFill = false
  OffsetIntersection = false
  OffsetJoinType = 0
  OffsetOpenResult = false
  PartialLoad = false
  Placement = pos=(0,0,-4) rot=(0,0,1;0rad)
  Refine = true
  Relative = true
  Support = -> [Sketch033[Edge2,Edge4,Edge7]]
  _Version = 2
FEATURE [PartDesign::SubShapeBinder] Binder002
  BindCopyOnChange = 0
  BindMode = 0
  ClaimChildren = false
  Context = -> Body002 [Binder002.]
  Fuse = false
  MakeFace = true
  OffsetFill = false
  OffsetIntersection = false
  OffsetJoinType = 0
  OffsetOpenResult = false
  PartialLoad = false
  Refine = true
  Relative = true
  Support = -> [Sketch033[Edge6,Edge5,Edge3]]
  _Version = 2
FEATURE [PartDesign::Pad] Pad
  BaseFeature = -> Pad009
  Direction = (0,0,1)
  Length = 4
  Length2 = 10
  Profile = -> Binder
  Refine = true
  Reversed = true
  Suppressed = false
  Type = 0
FEATURE [PartDesign::Pocket] Pocket011
  BaseFeature = -> Pad
  Direction = (0,0,-1)
  Length = 5
  Length2 = 5
  Profile = -> Binder002
  Refine = true
  Suppressed = false
  Type = 0
FEATURE [PartDesign::Pocket] Pocket012
  BaseFeature = -> Pocket011
  Direction = (0,0,-1)
  Length = 3
  Length2 = 5
  Profile = -> Binder001
  Refine = true
  Reversed = true
  Suppressed = false
  Type = 0
FEATURE [PartDesign::Body] Body002  label="Innendeckel"
  AllowCompound = false
  Group = -> [Sketch032,Pad007,Sketch033,Sketch035,Pad009,Binder,Binder001,Binder002,Pad,Pocket011,Pocket012]
  Origin = -> Origin002
  Placement = pos=(0,0,-0.3) rot=(0,0,1;0rad)
  Tip = -> Pocket012
FEATURE [PartDesign::Plane] DatumPlane
  AttachmentOffset = pos=(0,0,56) rot=(0,-1,0;0.715585rad)
  AttachmentSupport = -> [YZ_Plane006]
  Length = 139.092
  MapMode = 5
  Placement = pos=(56,0,0) rot=(0.840552,0.383062,0.383062;1.74363rad)
  ResizeMode = 0
  Width = 65.7088
FEATURE [Sketcher::SketchObject] Sketch050
  ArcFitTolerance = 1e-06
  AttachmentSupport = -> [DatumPlane]
  FullyConstrained = false
  MakeInternals = false
  MapMode = 5
  Placement = pos=(56,0,0) rot=(0.840552,0.383062,0.383062;1.74363rad)
  sketch-geometry (10):
    g0: LineSegment StartX=-43.0267 StartY=9.10069 StartZ=0 EndX=-43.0267 EndY=-0.899312 EndZ=0
    g1: LineSegment StartX=-42.0267 StartY=-1.89931 StartZ=0 EndX=-32.0267 EndY=-1.89931 EndZ=0
    g2: LineSegment StartX=-31.0267 StartY=-0.899312 StartZ=0 EndX=-31.0267 EndY=9.10069 EndZ=0
    g3: LineSegment StartX=-32.0267 StartY=10.1007 StartZ=0 EndX=-42.0267 EndY=10.1007 EndZ=0
    g4: ArcOfCircle CenterX=-42.0267 CenterY=9.10069 CenterZ=0 NormalX=0 NormalY=0 NormalZ=1 AngleXU=0 Radius=1 StartAngle=1.5708 EndAngle=3.14159
    g5: ArcOfCircle CenterX=-42.0267 CenterY=-0.899312 CenterZ=0 NormalX=0 NormalY=0 NormalZ=1 AngleXU=0 Radius=1 StartAngle=3.14159 EndAngle=4.71239
    g6: ArcOfCircle CenterX=-32.0267 CenterY=-0.899312 CenterZ=0 NormalX=0 NormalY=0 NormalZ=1 AngleXU=0 Radius=1 StartAngle=4.71239 EndAngle=6.28319
    g7: ArcOfCircle CenterX=-32.0267 CenterY=9.10069 CenterZ=0 NormalX=0 NormalY=0 NormalZ=1 AngleXU=0 Radius=1 StartAngle=-9e-16 EndAngle=1.5708
    g8: GeomPoint [constr] X=-43.0267 Y=10.1007 Z=0
    g9: GeomPoint [constr] X=-31.0267 Y=-1.89931 Z=0
  constraints (22):
    c: Tangent(g0,g4) = -1.5708
    c: Tangent(g0,g5) = -1.5708
    c: Tangent(g1,g5) = -1.5708
    c: Tangent(g1,g6) = -1.5708
    c: Tangent(g2,g6) = -1.5708
    c: Tangent(g2,g7) = -1.5708
    c: Tangent(g3,g7) = -1.5708
    c: Tangent(g3,g4) = -1.5708
    c: Vertical(g0)
    c: Vertical(g2)
    c: Horizontal(g1)
    c: Horizontal(g3)
    c: Equal(g4,g5)
    c: Equal(g5,g6)
    c: Equal(g6,g7)
    c: PointOnObject(g8,g0)
    c: PointOnObject(g8,g3)
    c: PointOnObject(g9,g1)
    c: PointOnObject(g9,g2)
    c: Radius(g5) = 1
    c: DistanceY(g1,g3) = 12
    c: DistanceX(g0,g2) = 12
FEATURE [PartDesign::Pocket] Pocket013
  BaseFeature = -> PolarPattern
  Direction = (-0.75471,0.656059,0)
  Length = 0
  Length2 = 5
  Midplane = true
  Placement = pos=(0,0,0) rot=(1,0,0;1.5708rad)
  Profile = -> Sketch050
  ReferenceAxis = -> Sketch050 [N_Axis]
  Refine = true
  Suppressed = false
  Type = 3
  UpToFace = -> PolarPattern [?Face53]
FEATURE [PartDesign::Plane] DatumPlane007
  AttachmentOffset = pos=(0,0,56) rot=(0,1,0;0.733038rad)
  AttachmentSupport = -> [YZ_Plane006]
  Length = 139.158
  MapMode = 5
  Placement = pos=(56,0,0) rot=(0.300294,0.674471,0.674471;2.55814rad)
  ResizeMode = 0
  Width = 65.7127
FEATURE [Sketcher::SketchObject] Sketch051
  ArcFitTolerance = 1e-06
  AttachmentSupport = -> [DatumPlane007]
  FullyConstrained = false
  MakeInternals = false
  MapMode = 5
  Placement = pos=(56,3.6e-15,0) rot=(0.300294,0.674471,0.674471;2.55814rad)
  sketch-geometry (10):
    g0: LineSegment StartX=32.074 StartY=6.65428 StartZ=0 EndX=32.074 EndY=0.654282 EndZ=0
    g1: LineSegment StartX=33.074 StartY=-0.345718 StartZ=0 EndX=46.074 EndY=-0.345718 EndZ=0
    g2: LineSegment StartX=47.074 StartY=0.654282 StartZ=0 EndX=47.074 EndY=6.65428 EndZ=0
    g3: LineSegment StartX=46.074 StartY=7.65428 StartZ=0 EndX=33.074 EndY=7.65428 EndZ=0
    g4: ArcOfCircle CenterX=33.074 CenterY=6.65428 CenterZ=0 NormalX=0 NormalY=0 NormalZ=1 AngleXU=0 Radius=1 StartAngle=1.5708 EndAngle=3.14159
    g5: ArcOfCircle CenterX=33.074 CenterY=0.654282 CenterZ=0 NormalX=0 NormalY=0 NormalZ=1 AngleXU=0 Radius=1 StartAngle=3.14159 EndAngle=4.71239
    g6: ArcOfCircle CenterX=46.074 CenterY=0.654282 CenterZ=0 NormalX=0 NormalY=0 NormalZ=1 AngleXU=0 Radius=1 StartAngle=4.71239 EndAngle=6.28319
    g7: ArcOfCircle CenterX=46.074 CenterY=6.65428 CenterZ=0 NormalX=0 NormalY=0 NormalZ=1 AngleXU=0 Radius=1 StartAngle=0 EndAngle=1.5708
    g8: GeomPoint [constr] X=32.074 Y=7.65428 Z=0
    g9: GeomPoint [constr] X=47.074 Y=-0.345718 Z=0
  constraints (22):
    c: Tangent(g0,g4) = -1.5708
    c: Tangent(g0,g5) = -1.5708
    c: Tangent(g1,g5) = -1.5708
    c: Tangent(g1,g6) = -1.5708
    c: Tangent(g2,g6) = -1.5708
    c: Tangent(g2,g7) = -1.5708
    c: Tangent(g3,g7) = -1.5708
    c: Tangent(g3,g4) = -1.5708
    c: Vertical(g0)
    c: Vertical(g2)
    c: Horizontal(g1)
    c: Horizontal(g3)
    c: Equal(g4,g5)
    c: Equal(g5,g6)
    c: Equal(g6,g7)
    c: PointOnObject(g8,g0)
    c: PointOnObject(g8,g3)
    c: PointOnObject(g9,g1)
    c: PointOnObject(g9,g2)
    c: Radius(g7) = 1
    c: DistanceX(g0,g2) = 15
    c: Distance(g1,g3) = 8
FEATURE [PartDesign::Pocket] Pocket014
  BaseFeature = -> Pocket013
  Direction = (-0.743145,-0.669131,-2e-16)
  Length = 0
  Length2 = 5
  Midplane = true
  Placement = pos=(0,0,0) rot=(1,0,0;1.5708rad)
  Profile = -> Sketch051
  ReferenceAxis = -> Sketch051 [N_Axis]
  Refine = true
  Suppressed = false
  Type = 3
  UpToFace = -> Pocket013 [Face67]
FEATURE [Sketcher::SketchObject] Sketch052
  ArcFitTolerance = 1e-06
  AttachmentSupport = -> [Pocket014]
  ExternalGeometry = -> [Pocket014]
  FullyConstrained = false
  MakeInternals = false
  MapMode = 5
  Placement = pos=(0,3.3e-15,10) rot=(1,0,0;3.14159rad)
  sketch-geometry (8):
    g0: ArcOfCircle CenterX=2.746e-13 CenterY=-3.287e-13 CenterZ=0 NormalX=0 NormalY=0 NormalZ=1 AngleXU=0 Radius=43.5 StartAngle=2.06214 EndAngle=2.3373
    g1: ArcOfCircle CenterX=-25.59 CenterY=35.1767 CenterZ=0 NormalX=0 NormalY=0 NormalZ=1 AngleXU=0 Radius=5.98 StartAngle=3.83931 EndAngle=5.00029
    g2: ArcOfCircle CenterX=-25.59 CenterY=35.1767 CenterZ=0 NormalX=0 NormalY=0 NormalZ=1 AngleXU=0 Radius=5.98 StartAngle=5.68233 EndAngle=6.84332
    g3: ArcOfCircle CenterX=-3.6e-15 CenterY=0 CenterZ=0 NormalX=0 NormalY=0 NormalZ=1 AngleXU=0 Radius=37.9171 StartAngle=2.14695 EndAngle=2.25249
    g4: LineSegment [constr] StartX=-25.59 StartY=35.1767 StartZ=0 EndX=-3.6e-15 EndY=0 EndZ=0
    g5: ArcOfCircle CenterX=2.746e-13 CenterY=-3.287e-13 CenterZ=0 NormalX=0 NormalY=0 NormalZ=1 AngleXU=0 Radius=43.5 StartAngle=2.3373 EndAngle=2.37054
    g6: ArcOfCircle CenterX=2.746e-13 CenterY=-3.287e-13 CenterZ=0 NormalX=0 NormalY=0 NormalZ=1 AngleXU=0 Radius=43.5 StartAngle=2.0289 EndAngle=2.06214
    g7: ArcOfCircle CenterX=-25.59 CenterY=35.1767 CenterZ=0 NormalX=0 NormalY=0 NormalZ=1 AngleXU=0 Radius=7.42182 StartAngle=3.85593 EndAngle=6.8267
  constraints (22):
    c: PointOnObject(g0,g-3)
    c: PointOnObject(g0,g1)
    c: PointOnObject(g0,g-4)
    c: Coincident(g0,g1)
    c: Coincident(g2,g1)
    c: Coincident(g2,g0)
    c: Coincident(g3,g-1)
    c: Coincident(g3,g1)
    c: Coincident(g3,g2)
    c: PointOnObject(g1,g0)
    c: Coincident(g4,g1)
    c: Coincident(g4,g3)
    c: Radius(g2) = 5.98
    c: PointOnObject(g1,g-3)
    c: Distance(g2,g1) = 4
    c: Coincident(g5,g0)
    c: Coincident(g5,g0)
    c: Coincident(g6,g0)
    c: Coincident(g6,g0)
    c: Coincident(g7,g1)
    c: Coincident(g7,g5)
    c: Coincident(g7,g6)
FEATURE [PartDesign::SubShapeBinder] Binder003
  BindCopyOnChange = 0
  BindMode = 0
  ClaimChildren = false
  Context = -> Body009 [Binder003.]
  Fuse = false
  MakeFace = true
  OffsetFill = false
  OffsetIntersection = false
  OffsetJoinType = 0
  OffsetOpenResult = false
  PartialLoad = false
  Placement = pos=(0,0,-6) rot=(0,0,1;0rad)
  Refine = true
  Relative = true
  Support = -> [Sketch052[Edge1,Edge4,Edge3,Edge2]]
  _Version = 2
FEATURE [PartDesign::SubShapeBinder] Binder004
  BindCopyOnChange = 0
  BindMode = 0
  ClaimChildren = false
  Context = -> Body009 [Binder004.]
  Fuse = false
  MakeFace = true
  OffsetFill = false
  OffsetIntersection = false
  OffsetJoinType = 0
  OffsetOpenResult = false
  PartialLoad = false
  Refine = true
  Relative = true
  Support = -> [Sketch052[Edge5,Edge6,Edge7,Edge4]]
  _Version = 2
FEATURE [PartDesign::Pad] Pad010
  BaseFeature = -> Pocket014
  Direction = (0,0,1)
  Length = 6
  Length2 = 10
  Placement = pos=(0,0,0) rot=(1,0,0;1.5708rad)
  Profile = -> Binder004
  Refine = true
  Reversed = true
  Suppressed = false
  Type = 0
FEATURE [PartDesign::Pad] Pad011
  BaseFeature = -> Pad010
  Direction = (0,0,1)
  Length = 16
  Length2 = 10
  Placement = pos=(0,0,0) rot=(1,0,0;1.5708rad)
  Profile = -> Binder003
  Refine = true
  Reversed = true
  Suppressed = false
  Type = 0
FEATURE [PartDesign::Body] Body009  label="Aussenhaut"
  AllowCompound = false
  Group = -> [Sketch045,Sketch044,AdditivePipe,Sketch046,Pocket008,DatumPlane005,DatumPlane006,Sketch047,Pocket001,Sketch048,Pocket009,Pocket010,Mirrored,Sketch049,PolarPattern,DatumPlane,Sketch050,Pocket013,DatumPlane007,Sketch051,Pocket014,Sketch052,Binder003,Binder004,Pad010,Pad011]
  Origin = -> Origin006
  Tip = -> Pad011
FEATURE [PartDesign::Pocket] Pocket
  BaseFeature = -> Revolution
  Direction = (0,0,1)
  Length = 5
  Length2 = 5
  Placement = pos=(0,0,0) rot=(1,0,0;1.5708rad)
  Profile = -> Sketch001
  ReferenceAxis = -> Sketch001 [N_Axis]
  Refine = true
  Suppressed = false
  Type = 0
FEATURE [PartDesign::Body] Body  label="Buzzerkopf"
  AllowCompound = false
  Group = -> [Sketch,Revolution,Sketch001,Pocket]
  Origin = -> Origin
  Placement = pos=(0,0,-0.6) rot=(0,0,1;5.02655rad)
  Tip = -> Pocket
